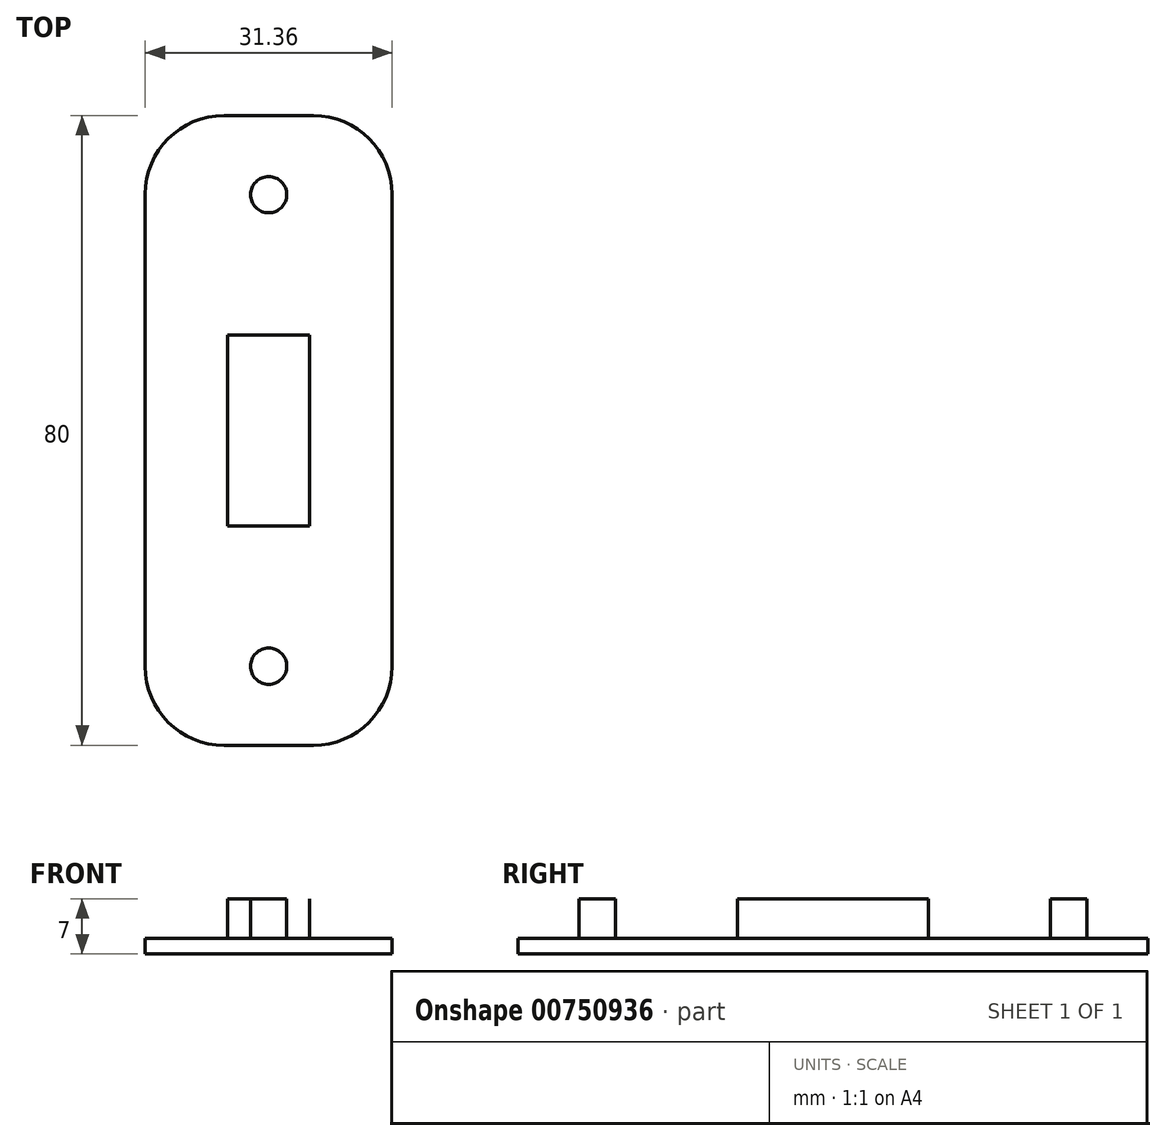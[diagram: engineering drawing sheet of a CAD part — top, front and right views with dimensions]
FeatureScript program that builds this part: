
annotation { "Feature Type Name" : "Feature", "Feature Type Description" : "" }
export const myFeature = defineFeature(function(context is Context, id is Id, definition is map)
    precondition{}
    {
        {
            var Q0;
            Q0=qCreatedBy(makeId("Top.planeOp"),FACE);
            var sketch = newSketch(context, id + "F0", { "sketchPlane" : qUnion([Q0])});
            skLineSegment(sketch, "E0.bottom", {"start": v(-15.68, 40) * mm, "end": v(15.68, 40) * mm});
            skLineSegment(sketch, "E0.top", {"start": v(-15.68, -40) * mm, "end": v(15.68, -40) * mm});
            skLineSegment(sketch, "E0.left", {"start": v(-15.68, 40) * mm, "end": v(-15.68, -40) * mm});
            skLineSegment(sketch, "E0.right", {"start": v(15.68, 40) * mm, "end": v(15.68, -40) * mm});
            skSolve(sketch);
        }
        {
            var Q0;
            Q0 = qSketchRegion(id + "F0", true);
            extrude(context, id + "F1", {"entities" : qUnion([Q0]), "depth" : 2 * mm, "offsetDistance" : 25 * mm});
        }
        {
            var Q0;
            Q0=makeQuery(id+"F1.opExtrude","CAP_FACE",FACE,{"disambiguationData":[OSD([sQuery(id+"F0.wireOp",EDGE,"E0.bottom"),sQuery(id+"F0.wireOp",EDGE,"E0.top"),sQuery(id+"F0.wireOp",EDGE,"E0.left"),sQuery(id+"F0.wireOp",EDGE,"E0.right")])],"isStart":false});
            var sketch = newSketch(context, id + "F2", { "sketchPlane" : qUnion([Q0])});
            skLineSegment(sketch, "E1.bottom", {"start": v(-5.2, 12.15) * mm, "end": v(5.2, 12.15) * mm});
            skLineSegment(sketch, "E1.top", {"start": v(-5.2, -12.15) * mm, "end": v(5.2, -12.15) * mm});
            skLineSegment(sketch, "E1.left", {"start": v(-5.2, 12.15) * mm, "end": v(-5.2, -12.15) * mm});
            skLineSegment(sketch, "E1.right", {"start": v(5.2, 12.15) * mm, "end": v(5.2, -12.15) * mm});
            skCircle(sketch, "E2", {"center": v(0, 29.95) * mm, "radius": 2.3 * mm});
            skCircle(sketch, "E3", {"center": v(0, -29.95) * mm, "radius": 2.3 * mm});
            skPoint(sketch, "E4", {"position": v(0, 32.25) * mm});
            skSolve(sketch);
        }
        {
            var Q0;
            Q0 = qSketchRegion(id + "F2", true);
            extrude(context, id + "F3", {"entities" : qUnion([Q0]), "operationType" : NewBodyOperationType.ADD, "depth" : 5 * mm, "offsetDistance" : 25 * mm});
        }
        {
            var Q0;
            Q0=makeQuery(id+"F1.opExtrude","SWEPT_EDGE",EDGE,{"disambiguationData":[OSD([sQuery(id+"F0.wireOp",EDGE,"E0.bottom"),sQuery(id+"F0.wireOp",EDGE,"E0.left")])]});
            var Q1;
            Q1=makeQuery(id+"F1.opExtrude","SWEPT_EDGE",EDGE,{"disambiguationData":[OSD([sQuery(id+"F0.wireOp",EDGE,"E0.bottom"),sQuery(id+"F0.wireOp",EDGE,"E0.right")])]});
            var Q2;
            Q2=makeQuery(id+"F1.opExtrude","SWEPT_EDGE",EDGE,{"disambiguationData":[OSD([sQuery(id+"F0.wireOp",EDGE,"E0.top"),sQuery(id+"F0.wireOp",EDGE,"E0.right")])]});
            var Q3;
            Q3=makeQuery(id+"F1.opExtrude","SWEPT_EDGE",EDGE,{"disambiguationData":[OSD([sQuery(id+"F0.wireOp",EDGE,"E0.top"),sQuery(id+"F0.wireOp",EDGE,"E0.left")])]});
            fillet(context, id + "F4", {"entities" : qUnion([Q0, Q1, Q2, Q3]), "radius" : 10 * mm, "tangentPropagation" : true, "allowEdgeOverflow" : false});
        }
    });
